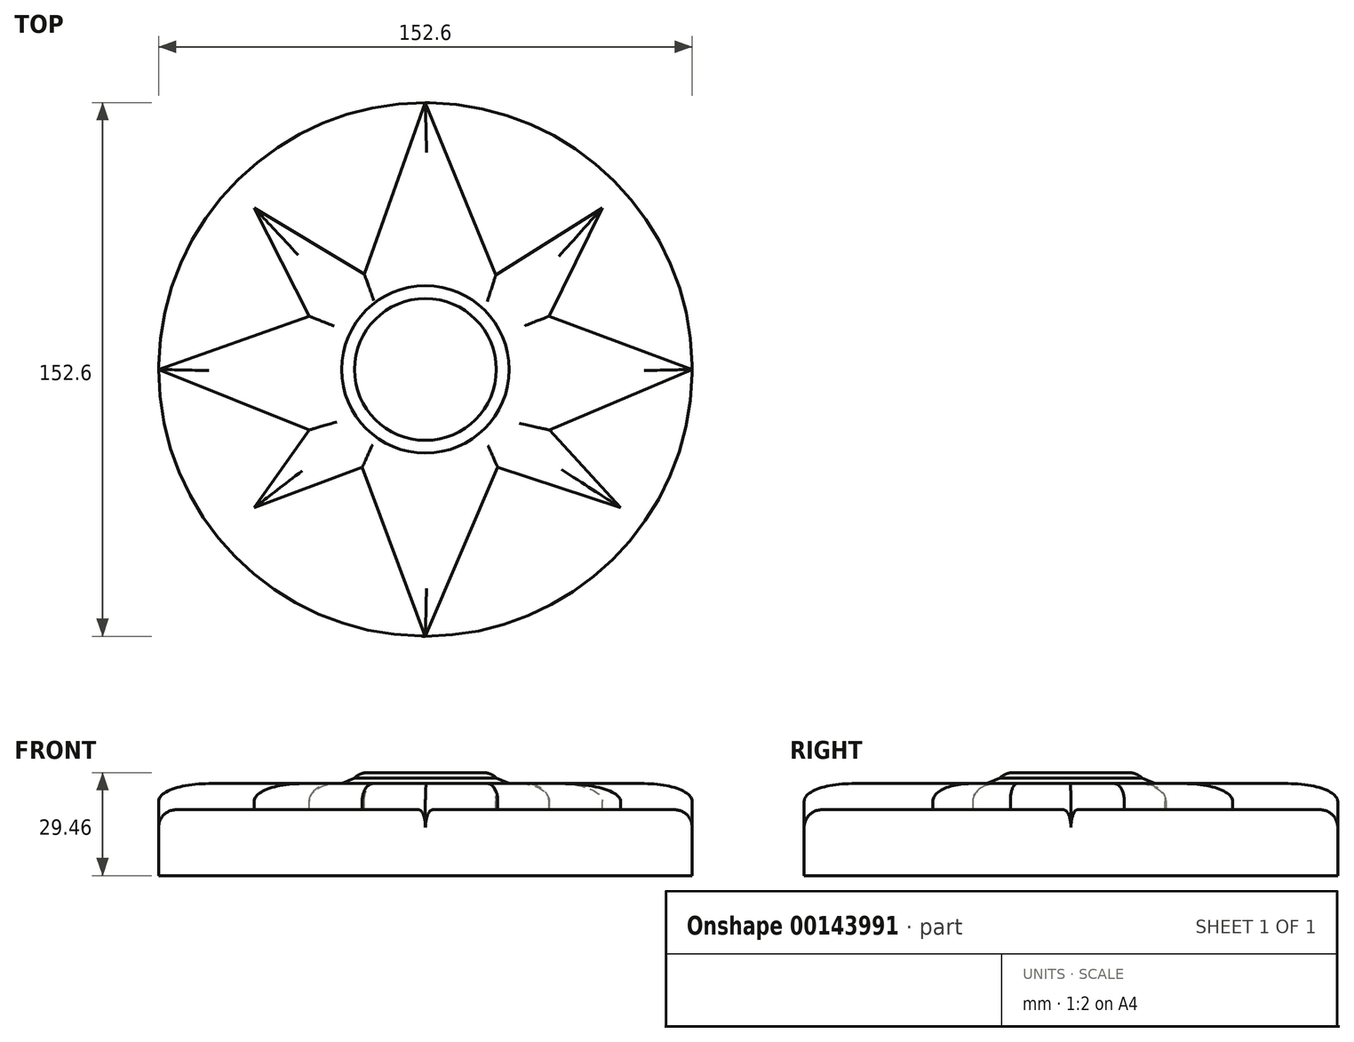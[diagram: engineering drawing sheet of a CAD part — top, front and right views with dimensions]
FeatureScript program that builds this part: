
annotation { "Feature Type Name" : "Feature", "Feature Type Description" : "" }
export const myFeature = defineFeature(function(context is Context, id is Id, definition is map)
    precondition{}
    {
        {
            var Q0;
            Q0=qCreatedBy(makeId("Top.planeOp"),FACE);
            var sketch = newSketch(context, id + "F0", { "sketchPlane" : qUnion([Q0])});
            skCircle(sketch, "E0", {"center": v(0, 0) * mm, "radius": 76.3 * mm});
            skSolve(sketch);
        }
        {
            var Q0;
            Q0=makeQuery(id+"F0.imprint","IMPRINT",FACE,{"disambiguationData":[TD([[makeQuery(id+"F0.imprint","IMPRINT",EDGE,{"derivedFrom":sQuery(id+"F0.wireOp",EDGE,"E0")}),1.0]])]});
            extrude(context, id + "F1", {"entities" : qUnion([Q0]), "depth" : 18.84 * mm});
        }
        {
            var Q0;
            Q0=makeQuery(id+"F1.opExtrude","CAP_FACE",FACE,{"disambiguationData":[OSD([sQuery(id+"F0.wireOp",EDGE,"E0")])],"isStart":false});
            var sketch = newSketch(context, id + "F2", { "sketchPlane" : qUnion([Q0])});
            skCircle(sketch, "E1", {"center": v(0, 0) * mm, "radius": 21.3 * mm});
            skSolve(sketch);
        }
        {
            var Q0;
            Q0=makeQuery(id+"F2.imprint","IMPRINT",FACE,{"disambiguationData":[TD([[makeQuery(id+"F2.imprint","IMPRINT",EDGE,{"derivedFrom":sQuery(id+"F2.wireOp",EDGE,"E1")}),1.0]])]});
            extrude(context, id + "F3", {"entities" : qUnion([Q0]), "operationType" : NewBodyOperationType.ADD, "depth" : 8.37 * mm});
        }
        {
            var Q0;
            Q0=makeQuery(id+"F1.opExtrude","CAP_FACE",FACE,{"disambiguationData":[OSD([sQuery(id+"F0.wireOp",EDGE,"E0")])],"isStart":false});
            var sketch = newSketch(context, id + "F4", { "sketchPlane" : qUnion([Q0])});
            skLineSegment(sketch, "E2", {"start": v(-20.08, 19.87) * mm, "end": v(0, 76.3) * mm});
            skLineSegment(sketch, "E3", {"start": v(0, 76.3) * mm, "end": v(23.01, 19.87) * mm});
            skLineSegment(sketch, "E4", {"start": v(23.01, 19.87) * mm, "end": v(76.3, 0) * mm});
            skLineSegment(sketch, "E5", {"start": v(76.3, 0) * mm, "end": v(23.01, -22.6) * mm});
            skLineSegment(sketch, "E6", {"start": v(23.01, -22.6) * mm, "end": v(0, -76.3) * mm});
            skLineSegment(sketch, "E7", {"start": v(0, -76.3) * mm, "end": v(-20.08, -22.6) * mm});
            skLineSegment(sketch, "E8", {"start": v(-20.08, -22.6) * mm, "end": v(-76.3, 0) * mm});
            skLineSegment(sketch, "E9", {"start": v(-76.3, 0) * mm, "end": v(-20.08, 19.87) * mm});
            skSolve(sketch);
        }
        {
            var Q0;
            Q0=makeQuery(id+"F4.imprint","IMPRINT",FACE,{"disambiguationData":[TD([[makeQuery(id+"F4.imprint","IMPRINT",EDGE,{"derivedFrom":sQuery(id+"F4.wireOp",EDGE,"E2")}),-1.0]])]});
            extrude(context, id + "F5", {"entities" : qUnion([Q0]), "operationType" : NewBodyOperationType.ADD, "depth" : 7.47 * mm});
        }
        {
            var Q0;
            Q0=makeQuery(id+"F3.opExtrude","CAP_FACE",FACE,{"disambiguationData":[OSD([sQuery(id+"F2.wireOp",EDGE,"E1")])],"isStart":false});
            var sketch = newSketch(context, id + "F6", { "sketchPlane" : qUnion([Q0])});
            skSolve(sketch);
        }
        {
            var Q0;
            Q0=makeQuery(id+"F6.imprint","IMPRINT",FACE,{"disambiguationData":[TD([[makeQuery(id+"F6.imprint","IMPRINT",EDGE,{"derivedFrom":makeQuery(id+"F3.opExtrude","CAP_EDGE",EDGE,{"disambiguationData":[OSD([sQuery(id+"F2.wireOp",EDGE,"E1")])],"isStart":false})}),1.0]])]});
            extrude(context, id + "F7", {"entities" : qUnion([Q0]), "operationType" : NewBodyOperationType.ADD, "depth" : 2.24 * mm});
        }
        {
            var Q0;
            Q0=makeQuery(id+"F5.opExtrude","CAP_FACE",FACE,{"disambiguationData":[OSD([sQuery(id+"F2.wireOp",EDGE,"E1"),sQuery(id+"F4.wireOp",EDGE,"E2"),sQuery(id+"F4.wireOp",EDGE,"E3"),sQuery(id+"F4.wireOp",EDGE,"E4"),sQuery(id+"F4.wireOp",EDGE,"E5"),sQuery(id+"F4.wireOp",EDGE,"E6"),sQuery(id+"F4.wireOp",EDGE,"E7"),sQuery(id+"F4.wireOp",EDGE,"E8"),sQuery(id+"F4.wireOp",EDGE,"E9")])],"isStart":false});
            var sketch = newSketch(context, id + "F8", { "sketchPlane" : qUnion([Q0])});
            skLineSegment(sketch, "E10", {"start": v(-17.45, 27.27) * mm, "end": v(-48.95, 46.23) * mm});
            skLineSegment(sketch, "E11", {"start": v(-48.95, 46.23) * mm, "end": v(-33.2, 15.24) * mm});
            skPoint(sketch, "E11.endSnap0", {"position": v(-33.2, 36.75) * mm});
            skLineSegment(sketch, "E12", {"start": v(-33.2, 15.24) * mm, "end": v(-20.08, 19.87) * mm});
            skLineSegment(sketch, "E13", {"start": v(-20.08, 19.87) * mm, "end": v(-17.45, 27.27) * mm});
            skLineSegment(sketch, "E14", {"start": v(20.12, 26.96) * mm, "end": v(50.63, 46.23) * mm});
            skLineSegment(sketch, "E15", {"start": v(50.63, 46.23) * mm, "end": v(35.37, 15.26) * mm});
            skPoint(sketch, "E15.endSnap0", {"position": v(35.37, 36.6) * mm});
            skLineSegment(sketch, "E16", {"start": v(35.37, 15.26) * mm, "end": v(23.01, 19.87) * mm});
            skLineSegment(sketch, "E17", {"start": v(23.01, 19.87) * mm, "end": v(20.12, 26.96) * mm});
            skSolve(sketch);
        }
        {
            var Q0;
            Q0=makeQuery(id+"F8.imprint","IMPRINT",FACE,{"disambiguationData":[TD([[makeQuery(id+"F8.imprint","IMPRINT",EDGE,{"derivedFrom":sQuery(id+"F8.wireOp",EDGE,"E10")}),1.0]])]});
            var Q1;
            Q1=makeQuery(id+"F8.imprint","IMPRINT",FACE,{"disambiguationData":[TD([[makeQuery(id+"F8.imprint","IMPRINT",EDGE,{"derivedFrom":sQuery(id+"F8.wireOp",EDGE,"E14")}),-1.0]])]});
            extrude(context, id + "F9", {"entities" : qUnion([Q0, Q1]), "operationType" : NewBodyOperationType.ADD, "oppositeDirection" : true, "depth" : 9.6 * mm});
        }
        {
            var Q0;
            Q0=makeQuery(id+"F9.boolean.opBoolean","MERGE",FACE,{"derivedFrom":[makeQuery(id+"F5.opExtrude","CAP_FACE",FACE,{"disambiguationData":[OSD([sQuery(id+"F2.wireOp",EDGE,"E1"),sQuery(id+"F4.wireOp",EDGE,"E2"),sQuery(id+"F4.wireOp",EDGE,"E3"),sQuery(id+"F4.wireOp",EDGE,"E4"),sQuery(id+"F4.wireOp",EDGE,"E5"),sQuery(id+"F4.wireOp",EDGE,"E6"),sQuery(id+"F4.wireOp",EDGE,"E7"),sQuery(id+"F4.wireOp",EDGE,"E8"),sQuery(id+"F4.wireOp",EDGE,"E9")])],"isStart":false}),makeQuery(id+"F9.opExtrude","CAP_FACE",FACE,{"disambiguationData":[OSD([sQuery(id+"F8.wireOp",EDGE,"E10"),sQuery(id+"F8.wireOp",EDGE,"E11"),sQuery(id+"F8.wireOp",EDGE,"E12"),sQuery(id+"F8.wireOp",EDGE,"E13")])],"isStart":true}),makeQuery(id+"F9.opExtrude","CAP_FACE",FACE,{"disambiguationData":[OSD([sQuery(id+"F8.wireOp",EDGE,"E14"),sQuery(id+"F8.wireOp",EDGE,"E15"),sQuery(id+"F8.wireOp",EDGE,"E16"),sQuery(id+"F8.wireOp",EDGE,"E17")])],"isStart":true})]});
            var sketch = newSketch(context, id + "F10", { "sketchPlane" : qUnion([Q0])});
            skLineSegment(sketch, "E18", {"start": v(-33.2, -17.32) * mm, "end": v(-48.95, -39.54) * mm});
            skLineSegment(sketch, "E19", {"start": v(-48.95, -39.54) * mm, "end": v(-18.07, -27.99) * mm});
            skSolve(sketch);
        }
        {
            var Q0;
            {var subQ0=sQuery(id+"F10.wireOp",EDGE,"E18");Q0=makeQuery(id+"F10.imprint","IMPRINT",FACE,{"disambiguationData":[TD([[makeQuery(id+"F10.imprint","IMPRINT",EDGE,{"derivedFrom":subQ0}),1.0]])]});}
            extrude(context, id + "F11", {"entities" : qUnion([Q0]), "operationType" : NewBodyOperationType.ADD, "oppositeDirection" : true, "depth" : 10.13 * mm});
        }
        {
            var Q0;
            {var subQ0=sQuery(id+"F4.wireOp",EDGE,"E8");var subQ1=sQuery(id+"F4.wireOp",EDGE,"E7");Q0=makeQuery(id+"F11.boolean.opBoolean","MERGE",FACE,{"derivedFrom":[makeQuery(id+"F9.boolean.opBoolean","MERGE",FACE,{"derivedFrom":[makeQuery(id+"F5.opExtrude","CAP_FACE",FACE,{"disambiguationData":[OSD([sQuery(id+"F2.wireOp",EDGE,"E1"),sQuery(id+"F4.wireOp",EDGE,"E2"),sQuery(id+"F4.wireOp",EDGE,"E3"),sQuery(id+"F4.wireOp",EDGE,"E4"),sQuery(id+"F4.wireOp",EDGE,"E5"),sQuery(id+"F4.wireOp",EDGE,"E6"),subQ1,subQ0,sQuery(id+"F4.wireOp",EDGE,"E9")])],"isStart":false}),makeQuery(id+"F9.opExtrude","CAP_FACE",FACE,{"disambiguationData":[OSD([sQuery(id+"F8.wireOp",EDGE,"E10"),sQuery(id+"F8.wireOp",EDGE,"E11"),sQuery(id+"F8.wireOp",EDGE,"E12"),sQuery(id+"F8.wireOp",EDGE,"E13")])],"isStart":true}),makeQuery(id+"F9.opExtrude","CAP_FACE",FACE,{"disambiguationData":[OSD([sQuery(id+"F8.wireOp",EDGE,"E14"),sQuery(id+"F8.wireOp",EDGE,"E15"),sQuery(id+"F8.wireOp",EDGE,"E16"),sQuery(id+"F8.wireOp",EDGE,"E17")])],"isStart":true})]}),makeQuery(id+"F11.opExtrude","CAP_FACE",FACE,{"disambiguationData":[OSD([subQ1,subQ0,sQuery(id+"F10.wireOp",EDGE,"E18"),sQuery(id+"F10.wireOp",EDGE,"E19")])],"isStart":true})]});}
            var sketch = newSketch(context, id + "F12", { "sketchPlane" : qUnion([Q0])});
            skLineSegment(sketch, "E20", {"start": v(35.45, -17.32) * mm, "end": v(55.84, -39.54) * mm});
            skPoint(sketch, "E20.endSnap0", {"position": v(55.84, 7.63) * mm});
            skLineSegment(sketch, "E21", {"start": v(55.84, -39.54) * mm, "end": v(20.7, -27.99) * mm});
            skSolve(sketch);
        }
        {
            var Q0;
            {var subQ0=sQuery(id+"F12.wireOp",EDGE,"E20");Q0=makeQuery(id+"F12.imprint","IMPRINT",FACE,{"disambiguationData":[TD([[makeQuery(id+"F12.imprint","IMPRINT",EDGE,{"derivedFrom":subQ0}),-1.0]])]});}
            extrude(context, id + "F13", {"entities" : qUnion([Q0]), "operationType" : NewBodyOperationType.ADD, "oppositeDirection" : true, "depth" : 8.34 * mm});
        }
        {
            var Q0;
            Q0=makeQuery(id+"F5.opExtrude","CAP_EDGE",EDGE,{"disambiguationData":[OSD([sQuery(id+"F4.wireOp",EDGE,"E7")])],"isStart":false});
            var Q1;
            Q1=makeQuery(id+"F11.opExtrude","CAP_EDGE",EDGE,{"disambiguationData":[OSD([sQuery(id+"F10.wireOp",EDGE,"E19")])],"isStart":true});
            var Q2;
            Q2=makeQuery(id+"F11.opExtrude","CAP_EDGE",EDGE,{"disambiguationData":[OSD([sQuery(id+"F10.wireOp",EDGE,"E18")])],"isStart":true});
            var Q3;
            Q3=makeQuery(id+"F5.opExtrude","CAP_EDGE",EDGE,{"disambiguationData":[OSD([sQuery(id+"F4.wireOp",EDGE,"E8")])],"isStart":false});
            var Q4;
            Q4=makeQuery(id+"F5.opExtrude","CAP_EDGE",EDGE,{"disambiguationData":[OSD([sQuery(id+"F4.wireOp",EDGE,"E9")])],"isStart":false});
            var Q5;
            Q5=makeQuery(id+"F9.opExtrude","CAP_EDGE",EDGE,{"disambiguationData":[OSD([sQuery(id+"F8.wireOp",EDGE,"E11")])],"isStart":true});
            var Q6;
            Q6=makeQuery(id+"F9.opExtrude","CAP_EDGE",EDGE,{"disambiguationData":[OSD([sQuery(id+"F8.wireOp",EDGE,"E10")])],"isStart":true});
            var Q7;
            Q7=makeQuery(id+"F5.opExtrude","CAP_EDGE",EDGE,{"disambiguationData":[OSD([sQuery(id+"F4.wireOp",EDGE,"E2")])],"isStart":false});
            var Q8;
            Q8=makeQuery(id+"F5.opExtrude","CAP_EDGE",EDGE,{"disambiguationData":[OSD([sQuery(id+"F4.wireOp",EDGE,"E3")])],"isStart":false});
            var Q9;
            Q9=makeQuery(id+"F9.opExtrude","CAP_EDGE",EDGE,{"disambiguationData":[OSD([sQuery(id+"F8.wireOp",EDGE,"E14")])],"isStart":true});
            var Q10;
            Q10=makeQuery(id+"F9.opExtrude","CAP_EDGE",EDGE,{"disambiguationData":[OSD([sQuery(id+"F8.wireOp",EDGE,"E15")])],"isStart":true});
            var Q11;
            Q11=makeQuery(id+"F5.opExtrude","CAP_EDGE",EDGE,{"disambiguationData":[OSD([sQuery(id+"F4.wireOp",EDGE,"E4")])],"isStart":false});
            var Q12;
            Q12=makeQuery(id+"F5.opExtrude","CAP_EDGE",EDGE,{"disambiguationData":[OSD([sQuery(id+"F4.wireOp",EDGE,"E5")])],"isStart":false});
            var Q13;
            Q13=makeQuery(id+"F13.opExtrude","CAP_EDGE",EDGE,{"disambiguationData":[OSD([sQuery(id+"F12.wireOp",EDGE,"E20")])],"isStart":true});
            var Q14;
            Q14=makeQuery(id+"F13.opExtrude","CAP_EDGE",EDGE,{"disambiguationData":[OSD([sQuery(id+"F12.wireOp",EDGE,"E21")])],"isStart":true});
            var Q15;
            Q15=makeQuery(id+"F5.opExtrude","CAP_EDGE",EDGE,{"disambiguationData":[OSD([sQuery(id+"F4.wireOp",EDGE,"E6")])],"isStart":false});
            var Q16;
            {var subQ0=sQuery(id+"F0.wireOp",EDGE,"E0");Q16=makeQuery(id+"F5.boolean.opBoolean","SPLIT",EDGE,{"disambiguationData":[TD([makeQuery(id+"F1.opExtrude","SWEPT_FACE",FACE,{"disambiguationData":[OSD([subQ0])]}),makeQuery(id+"F1.opExtrude","CAP_FACE",FACE,{"disambiguationData":[OSD([subQ0])],"isStart":false}),makeQuery(id+"F5.opExtrude","SWEPT_FACE",FACE,{"disambiguationData":[OSD([sQuery(id+"F4.wireOp",EDGE,"E6")])]}),makeQuery(id+"F5.opExtrude","SWEPT_FACE",FACE,{"disambiguationData":[OSD([sQuery(id+"F4.wireOp",EDGE,"E7")])]}),makeQuery(id+"F5.opExtrude","SWEPT_FACE",FACE,{"disambiguationData":[OSD([sQuery(id+"F4.wireOp",EDGE,"E8")])]}),makeQuery(id+"F5.opExtrude","SWEPT_FACE",FACE,{"disambiguationData":[OSD([sQuery(id+"F4.wireOp",EDGE,"E9")])]})])],"derivedFrom":makeQuery(id+"F1.opExtrude","CAP_EDGE",EDGE,{"disambiguationData":[OSD([subQ0])],"isStart":false})});}
            var Q17;
            {var subQ0=sQuery(id+"F0.wireOp",EDGE,"E0");Q17=makeQuery(id+"F5.boolean.opBoolean","SPLIT",EDGE,{"disambiguationData":[TD([makeQuery(id+"F1.opExtrude","SWEPT_FACE",FACE,{"disambiguationData":[OSD([subQ0])]}),makeQuery(id+"F1.opExtrude","CAP_FACE",FACE,{"disambiguationData":[OSD([subQ0])],"isStart":false}),makeQuery(id+"F5.opExtrude","SWEPT_FACE",FACE,{"disambiguationData":[OSD([sQuery(id+"F4.wireOp",EDGE,"E2")])]}),makeQuery(id+"F5.opExtrude","SWEPT_FACE",FACE,{"disambiguationData":[OSD([sQuery(id+"F4.wireOp",EDGE,"E3")])]}),makeQuery(id+"F5.opExtrude","SWEPT_FACE",FACE,{"disambiguationData":[OSD([sQuery(id+"F4.wireOp",EDGE,"E8")])]}),makeQuery(id+"F5.opExtrude","SWEPT_FACE",FACE,{"disambiguationData":[OSD([sQuery(id+"F4.wireOp",EDGE,"E9")])]})])],"derivedFrom":makeQuery(id+"F1.opExtrude","CAP_EDGE",EDGE,{"disambiguationData":[OSD([subQ0])],"isStart":false})});}
            var Q18;
            {var subQ0=sQuery(id+"F0.wireOp",EDGE,"E0");Q18=makeQuery(id+"F5.boolean.opBoolean","SPLIT",EDGE,{"disambiguationData":[TD([makeQuery(id+"F1.opExtrude","SWEPT_FACE",FACE,{"disambiguationData":[OSD([subQ0])]}),makeQuery(id+"F1.opExtrude","CAP_FACE",FACE,{"disambiguationData":[OSD([subQ0])],"isStart":false}),makeQuery(id+"F5.opExtrude","SWEPT_FACE",FACE,{"disambiguationData":[OSD([sQuery(id+"F4.wireOp",EDGE,"E2")])]}),makeQuery(id+"F5.opExtrude","SWEPT_FACE",FACE,{"disambiguationData":[OSD([sQuery(id+"F4.wireOp",EDGE,"E3")])]}),makeQuery(id+"F5.opExtrude","SWEPT_FACE",FACE,{"disambiguationData":[OSD([sQuery(id+"F4.wireOp",EDGE,"E4")])]}),makeQuery(id+"F5.opExtrude","SWEPT_FACE",FACE,{"disambiguationData":[OSD([sQuery(id+"F4.wireOp",EDGE,"E5")])]})])],"derivedFrom":makeQuery(id+"F1.opExtrude","CAP_EDGE",EDGE,{"disambiguationData":[OSD([subQ0])],"isStart":false})});}
            var Q19;
            {var subQ0=sQuery(id+"F0.wireOp",EDGE,"E0");Q19=makeQuery(id+"F5.boolean.opBoolean","SPLIT",EDGE,{"disambiguationData":[TD([makeQuery(id+"F1.opExtrude","SWEPT_FACE",FACE,{"disambiguationData":[OSD([subQ0])]}),makeQuery(id+"F1.opExtrude","CAP_FACE",FACE,{"disambiguationData":[OSD([subQ0])],"isStart":false}),makeQuery(id+"F5.opExtrude","SWEPT_FACE",FACE,{"disambiguationData":[OSD([sQuery(id+"F4.wireOp",EDGE,"E4")])]}),makeQuery(id+"F5.opExtrude","SWEPT_FACE",FACE,{"disambiguationData":[OSD([sQuery(id+"F4.wireOp",EDGE,"E5")])]}),makeQuery(id+"F5.opExtrude","SWEPT_FACE",FACE,{"disambiguationData":[OSD([sQuery(id+"F4.wireOp",EDGE,"E6")])]}),makeQuery(id+"F5.opExtrude","SWEPT_FACE",FACE,{"disambiguationData":[OSD([sQuery(id+"F4.wireOp",EDGE,"E7")])]})])],"derivedFrom":makeQuery(id+"F1.opExtrude","CAP_EDGE",EDGE,{"disambiguationData":[OSD([subQ0])],"isStart":false})});}
            var Q20;
            Q20=makeQuery(id+"F7.opExtrude","CAP_EDGE",EDGE,{"disambiguationData":[OSD([sQuery(id+"F2.wireOp",EDGE,"E1")])],"isStart":false});
            fillet(context, id + "F14", {"entities" : qUnion([Q0, Q1, Q2, Q3, Q4, Q5, Q6, Q7, Q8, Q9, Q10, Q11, Q12, Q13, Q14, Q15, Q16, Q17, Q18, Q19, Q20]), "radius" : 5.08 * mm, "tangentPropagation" : true, "allowEdgeOverflow" : false});
        }
        {
            var Q0;
            Q0=makeQuery(id+"F14.opFillet","BLEND_FACE",FACE,{"disambiguationData":[OSD([sQuery(id+"F2.wireOp",EDGE,"E1")])]});
            chamfer(context, id + "F15", {"entities" : qUnion([Q0]), "width" : 5.08 * mm, "tangentPropagation" : true});
        }
    });
